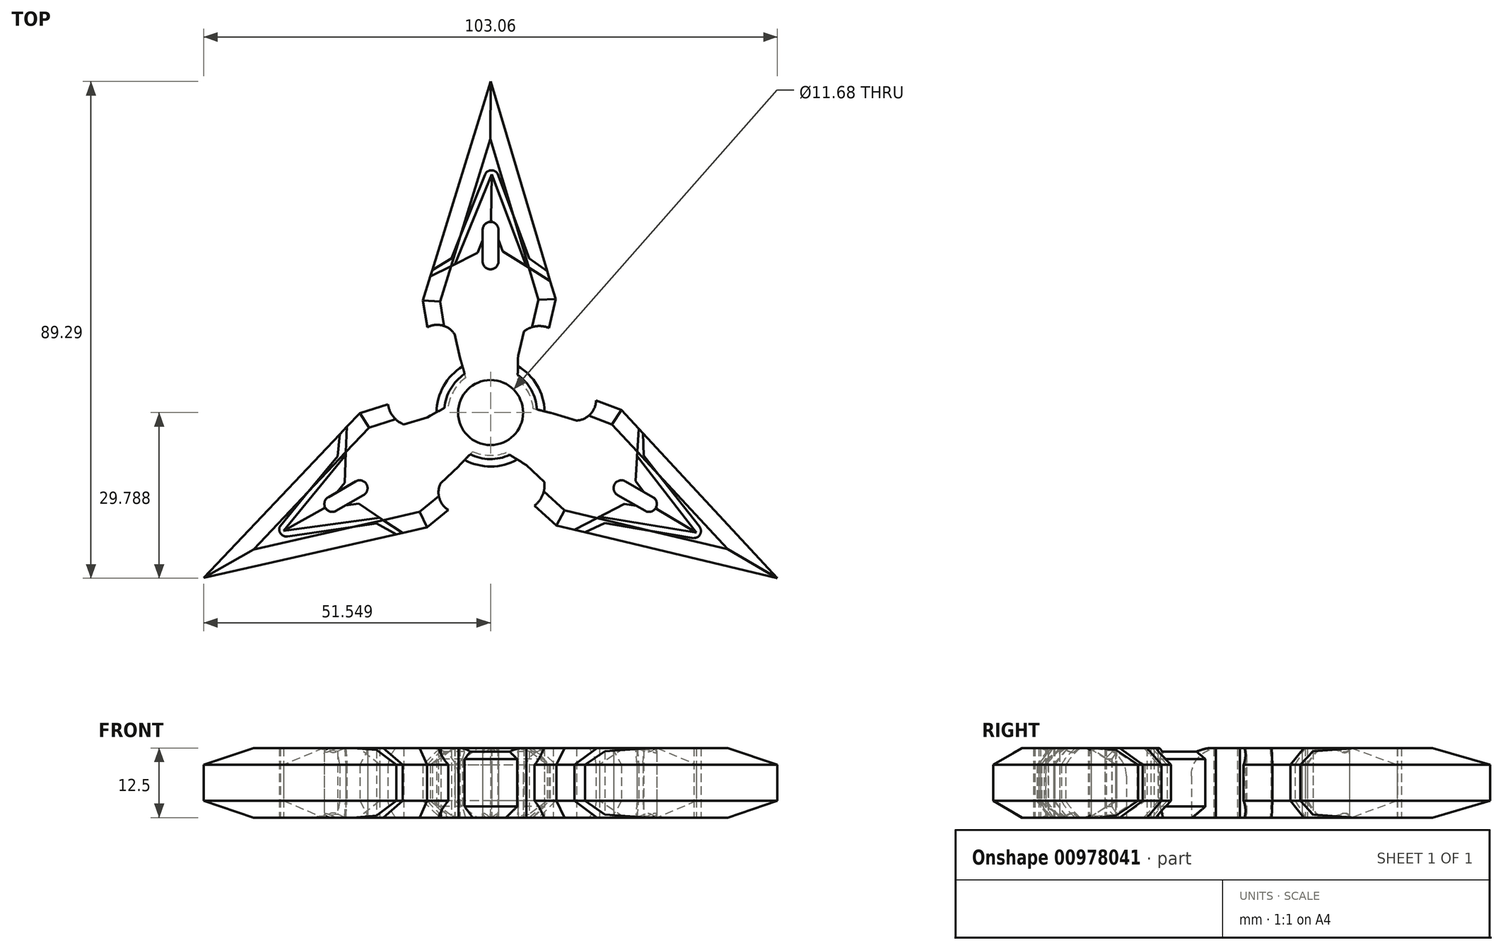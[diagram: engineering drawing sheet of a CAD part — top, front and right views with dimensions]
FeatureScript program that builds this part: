
annotation { "Feature Type Name" : "Feature", "Feature Type Description" : "" }
export const myFeature = defineFeature(function(context is Context, id is Id, definition is map)
    precondition{}
    {
        {
            var Q0;
            Q0=qCreatedBy(makeId("Top.planeOp"),FACE);
            var sketch = newSketch(context, id + "F0", { "sketchPlane" : qUnion([Q0])});
            skLineSegment(sketch, "E0", {"start": v(-184.92, 71.1) * mm, "end": v(-185.7, 75.95) * mm});
            skLineSegment(sketch, "E1", {"start": v(-185.7, 75.95) * mm, "end": v(-173.5, 115.3) * mm});
            skLineSegment(sketch, "E2", {"start": v(-173.5, 115.3) * mm, "end": v(-161.88, 76.16) * mm});
            skLineSegment(sketch, "E3", {"start": v(-161.88, 76.16) * mm, "end": v(-163.03, 71) * mm});
            skLineSegment(sketch, "E4", {"start": v(-167.58, 70.37) * mm, "end": v(-168.6, 66.06) * mm});
            skArc(sketch, "E5", {"start": v(-180.03, 69.88) * mm, "mid": v(-182.23, 71.45) * mm, "end": v(-184.92, 71.1) * mm});
            skArc(sketch, "E6", {"start": v(-163.03, 71) * mm, "mid": v(-165.39, 71.3) * mm, "end": v(-167.58, 70.37) * mm});
            skLineSegment(sketch, "E7", {"start": v(-180.03, 69.88) * mm, "end": v(-179.04, 65.65) * mm});
            skLineSegment(sketch, "E8.left", {"start": v(-172.13, 82.95) * mm, "end": v(-172.13, 88.64) * mm});
            skLineSegment(sketch, "E8.right", {"start": v(-174.97, 82.95) * mm, "end": v(-174.97, 88.64) * mm});
            skPoint(sketch, "E8.middle", {"position": v(-173.55, 85.8) * mm});
            skArc(sketch, "E9", {"start": v(-172.13, 88.64) * mm, "mid": v(-173.55, 90.06) * mm, "end": v(-174.97, 88.64) * mm});
            skArc(sketch, "E10", {"start": v(-174.97, 82.95) * mm, "mid": v(-173.55, 81.53) * mm, "end": v(-172.13, 82.95) * mm});
            skLineSegment(sketch, "E11", {"start": v(-184.36, 80.28) * mm, "end": v(-179.97, 82.46) * mm});
            skLineSegment(sketch, "E12", {"start": v(-179.97, 82.46) * mm, "end": v(-173.35, 98.59) * mm});
            skLineSegment(sketch, "E13", {"start": v(-173.35, 98.59) * mm, "end": v(-167.13, 82.12) * mm});
            skLineSegment(sketch, "E14", {"start": v(-167.13, 82.12) * mm, "end": v(-162.84, 79.4) * mm});
            skLineSegment(sketch, "E15", {"start": v(-162.84, 79.4) * mm, "end": v(-163.38, 81.23) * mm});
            skLineSegment(sketch, "E16", {"start": v(-163.38, 81.23) * mm, "end": v(-166.6, 83.5) * mm});
            skLineSegment(sketch, "E17", {"start": v(-166.6, 83.5) * mm, "end": v(-172.28, 98.69) * mm});
            skLineSegment(sketch, "E18", {"start": v(-184.02, 81.38) * mm, "end": v(-180.6, 83.48) * mm});
            skLineSegment(sketch, "E19", {"start": v(-180.6, 83.48) * mm, "end": v(-174.57, 98.54) * mm});
            skArc(sketch, "E20", {"start": v(-172.28, 98.69) * mm, "mid": v(-173.47, 99.33) * mm, "end": v(-174.57, 98.54) * mm});
            skArc(sketch, "E21", {"start": v(-178.6, 64.07) * mm, "mid": v(-181.98, 60.57) * mm, "end": v(-183.24, 55.86) * mm});
            skPoint(sketch, "E21.centerSnap0", {"position": v(-173.55, 81.53) * mm});
            skLineSegment(sketch, "E22.1.0", {"start": v(-184.94, 35.18) * mm, "end": v(-225.1, 26.07) * mm});
            skPoint(sketch, "E22.1.1", {"position": v(-195.84, 42.92) * mm});
            skPoint(sketch, "E22.1.3", {"position": v(-199.54, 40.78) * mm});
            skLineSegment(sketch, "E22.1.4", {"start": v(-201.02, 47.96) * mm, "end": v(-211.34, 35.44) * mm});
            skLineSegment(sketch, "E22.1.5", {"start": v(-225.1, 26.07) * mm, "end": v(-197.03, 55.71) * mm});
            skLineSegment(sketch, "E22.1.6", {"start": v(-194.02, 35.84) * mm, "end": v(-210.06, 33.53) * mm});
            skLineSegment(sketch, "E22.1.7", {"start": v(-210.72, 34.56) * mm, "end": v(-199.56, 48.18) * mm});
            skLineSegment(sketch, "E22.1.8", {"start": v(-189.17, 53.67) * mm, "end": v(-184.92, 54.94) * mm});
            skLineSegment(sketch, "E22.1.9", {"start": v(-193.44, 36.9) * mm, "end": v(-210.72, 34.56) * mm});
            skLineSegment(sketch, "E22.1.10", {"start": v(-197.03, 55.71) * mm, "end": v(-191.99, 57.29) * mm});
            skArc(sketch, "E22.1.11", {"start": v(-182.52, 43.14) * mm, "mid": v(-182.77, 40.44) * mm, "end": v(-181.13, 38.28) * mm});
            skArc(sketch, "E22.1.12", {"start": v(-191.99, 57.29) * mm, "mid": v(-191.07, 55.1) * mm, "end": v(-189.17, 53.67) * mm});
            skLineSegment(sketch, "E22.1.13", {"start": v(-190.48, 33.92) * mm, "end": v(-194.02, 35.84) * mm});
            skLineSegment(sketch, "E22.1.14", {"start": v(-200.67, 51.87) * mm, "end": v(-201.02, 47.96) * mm});
            skLineSegment(sketch, "E22.1.15", {"start": v(-181.13, 38.28) * mm, "end": v(-184.94, 35.18) * mm});
            skLineSegment(sketch, "E22.1.16", {"start": v(-189.36, 34.18) * mm, "end": v(-193.44, 36.9) * mm});
            skLineSegment(sketch, "E22.1.17", {"start": v(-182.52, 43.14) * mm, "end": v(-179.34, 46.1) * mm});
            skArc(sketch, "E22.1.18", {"start": v(-211.34, 35.44) * mm, "mid": v(-211.3, 34.09) * mm, "end": v(-210.06, 33.53) * mm});
            skLineSegment(sketch, "E22.1.19", {"start": v(-199.56, 48.18) * mm, "end": v(-199.36, 53.26) * mm});
            skLineSegment(sketch, "E22.1.20", {"start": v(-199.36, 53.26) * mm, "end": v(-200.67, 51.87) * mm});
            skLineSegment(sketch, "E22.1.21", {"start": v(-197.79, 43.44) * mm, "end": v(-202.71, 40.6) * mm});
            skArc(sketch, "E22.1.22", {"start": v(-202.71, 40.6) * mm, "mid": v(-203.23, 38.65) * mm, "end": v(-201.29, 38.13) * mm});
            skLineSegment(sketch, "E22.1.23", {"start": v(-196.37, 40.98) * mm, "end": v(-201.29, 38.13) * mm});
            skArc(sketch, "E22.1.24", {"start": v(-196.37, 40.98) * mm, "mid": v(-195.84, 42.92) * mm, "end": v(-197.79, 43.44) * mm});
            skLineSegment(sketch, "E22.2.0", {"start": v(-150.01, 56.23) * mm, "end": v(-122.04, 26) * mm});
            skPoint(sketch, "E22.2.1", {"position": v(-151.26, 42.92) * mm});
            skPoint(sketch, "E22.2.3", {"position": v(-147.56, 40.78) * mm});
            skLineSegment(sketch, "E22.2.4", {"start": v(-153.04, 35.9) * mm, "end": v(-137.04, 33.24) * mm});
            skLineSegment(sketch, "E22.2.5", {"start": v(-122.04, 26) * mm, "end": v(-161.74, 35.5) * mm});
            skLineSegment(sketch, "E22.2.6", {"start": v(-146.04, 48.04) * mm, "end": v(-136.02, 35.3) * mm});
            skLineSegment(sketch, "E22.2.7", {"start": v(-136.58, 34.22) * mm, "end": v(-153.96, 37.06) * mm});
            skLineSegment(sketch, "E22.2.8", {"start": v(-163.9, 43.32) * mm, "end": v(-167.13, 46.37) * mm});
            skLineSegment(sketch, "E22.2.9", {"start": v(-147.24, 48.01) * mm, "end": v(-136.58, 34.22) * mm});
            skLineSegment(sketch, "E22.2.10", {"start": v(-161.74, 35.5) * mm, "end": v(-165.63, 39.07) * mm});
            skArc(sketch, "E22.2.11", {"start": v(-158.11, 54.35) * mm, "mid": v(-155.65, 55.48) * mm, "end": v(-154.6, 57.98) * mm});
            skArc(sketch, "E22.2.12", {"start": v(-165.63, 39.07) * mm, "mid": v(-164.2, 40.96) * mm, "end": v(-163.9, 43.32) * mm});
            skLineSegment(sketch, "E22.2.13", {"start": v(-146.15, 52.06) * mm, "end": v(-146.04, 48.04) * mm});
            skLineSegment(sketch, "E22.2.14", {"start": v(-156.6, 34.26) * mm, "end": v(-153.04, 35.9) * mm});
            skLineSegment(sketch, "E22.2.15", {"start": v(-154.6, 57.98) * mm, "end": v(-150.01, 56.23) * mm});
            skLineSegment(sketch, "E22.2.16", {"start": v(-146.93, 52.9) * mm, "end": v(-147.24, 48.01) * mm});
            skLineSegment(sketch, "E22.2.17", {"start": v(-158.11, 54.35) * mm, "end": v(-162.27, 55.61) * mm});
            skArc(sketch, "E22.2.18", {"start": v(-137.04, 33.24) * mm, "mid": v(-135.88, 33.95) * mm, "end": v(-136.02, 35.3) * mm});
            skLineSegment(sketch, "E22.2.19", {"start": v(-153.96, 37.06) * mm, "end": v(-158.46, 34.7) * mm});
            skLineSegment(sketch, "E22.2.20", {"start": v(-158.46, 34.7) * mm, "end": v(-156.6, 34.26) * mm});
            skLineSegment(sketch, "E22.2.21", {"start": v(-150.74, 40.98) * mm, "end": v(-145.81, 38.13) * mm});
            skArc(sketch, "E22.2.22", {"start": v(-145.81, 38.13) * mm, "mid": v(-143.87, 38.65) * mm, "end": v(-144.4, 40.6) * mm});
            skLineSegment(sketch, "E22.2.23", {"start": v(-149.32, 43.44) * mm, "end": v(-144.4, 40.6) * mm});
            skArc(sketch, "E22.2.24", {"start": v(-149.32, 43.44) * mm, "mid": v(-151.26, 42.92) * mm, "end": v(-150.74, 40.98) * mm});
            skLineSegment(sketch, "E23", {"start": v(-184.92, 54.94) * mm, "end": v(-183.24, 55.86) * mm});
            skLineSegment(sketch, "E24", {"start": v(-179.34, 46.1) * mm, "end": v(-178.2, 47.28) * mm});
            skLineSegment(sketch, "E25.1.0", {"start": v(-167.13, 46.37) * mm, "end": v(-168.77, 47.36) * mm});
            skLineSegment(sketch, "E25.1.1", {"start": v(-162.27, 55.61) * mm, "end": v(-163.86, 56.01) * mm});
            skLineSegment(sketch, "E25.2.0", {"start": v(-168.6, 66.06) * mm, "end": v(-168.64, 64.15) * mm});
            skLineSegment(sketch, "E25.2.1", {"start": v(-179.04, 65.65) * mm, "end": v(-178.6, 64.07) * mm});
            skArc(sketch, "E26.trimOffspring", {"start": v(-178.2, 47.28) * mm, "mid": v(-173.47, 46.1) * mm, "end": v(-168.77, 47.36) * mm});
            skArc(sketch, "E27.trimOffspring", {"start": v(-163.86, 56.01) * mm, "mid": v(-165.2, 60.7) * mm, "end": v(-168.64, 64.15) * mm});
            skSolve(sketch);
        }
        {
            var Q0;
            {var subQ10=sQuery(id+"F0.wireOp",EDGE,"E0");Q0=makeQuery(id+"F0.imprint","IMPRINT",FACE,{"disambiguationData":[TD([[makeQuery(id+"F0.imprint","IMPRINT",EDGE,{"derivedFrom":subQ10}),-1.0]])]});}
            var Q1;
            {var subQ0=sQuery(id+"F0.wireOp",EDGE,"E16");Q1=makeQuery(id+"F0.imprint","IMPRINT",FACE,{"disambiguationData":[TD([[makeQuery(id+"F0.imprint","IMPRINT",EDGE,{"derivedFrom":subQ0}),-1.0]])]});}
            var Q2;
            Q2=makeQuery(id+"F0.imprint","IMPRINT",FACE,{"disambiguationData":[TD([[makeQuery(id+"F0.imprint","IMPRINT",EDGE,{"derivedFrom":sQuery(id+"F0.wireOp",EDGE,"E22.2.4")}),-1.0]])]});
            var Q3;
            Q3=makeQuery(id+"F0.imprint","IMPRINT",FACE,{"disambiguationData":[TD([[makeQuery(id+"F0.imprint","IMPRINT",EDGE,{"derivedFrom":sQuery(id+"F0.wireOp",EDGE,"E22.1.4")}),-1.0]])]});
            extrude(context, id + "F1", {"entities" : qUnion([Q0, Q1, Q2, Q3]), "depth" : 12.5 * mm, "offsetDistance" : 25 * mm});
        }
        {
            var Q0;
            {var subQ0=sQuery(id+"F0.wireOp",EDGE,"E22.1.0");Q0=makeQuery(id+"F1.opExtrude","CAP_EDGE",EDGE,{"disambiguationData":[OSD([subQ0]),TDD([makeQuery(id+"F0.imprint","IMPRINT",EDGE,{"disambiguationData":[TD([[makeQuery(id+"F0.imprint","INTERSECT",VERTEX,{"derivedFrom":[subQ0,sQuery(id+"F0.wireOp",EDGE,"E22.1.13")]}),-1.0]])],"derivedFrom":subQ0})])],"isStart":false});}
            var Q1;
            {var subQ0=sQuery(id+"F0.wireOp",EDGE,"E22.1.5");Q1=makeQuery(id+"F1.opExtrude","CAP_EDGE",EDGE,{"disambiguationData":[OSD([subQ0]),TDD([makeQuery(id+"F0.imprint","IMPRINT",EDGE,{"disambiguationData":[TD([[makeQuery(id+"F0.imprint","INTERSECT",VERTEX,{"derivedFrom":[sQuery(id+"F0.wireOp",EDGE,"E22.1.0"),subQ0]}),-1.0]])],"derivedFrom":subQ0})])],"isStart":false});}
            var Q2;
            {var subQ0=sQuery(id+"F0.wireOp",EDGE,"E22.2.5");Q2=makeQuery(id+"F1.opExtrude","CAP_EDGE",EDGE,{"disambiguationData":[OSD([subQ0]),TDD([makeQuery(id+"F0.imprint","IMPRINT",EDGE,{"disambiguationData":[TD([[makeQuery(id+"F0.imprint","INTERSECT",VERTEX,{"derivedFrom":[sQuery(id+"F0.wireOp",EDGE,"E22.2.0"),subQ0]}),-1.0]])],"derivedFrom":subQ0})])],"isStart":false});}
            var Q3;
            {var subQ0=sQuery(id+"F0.wireOp",EDGE,"E22.2.0");Q3=makeQuery(id+"F1.opExtrude","CAP_EDGE",EDGE,{"disambiguationData":[OSD([subQ0]),TDD([makeQuery(id+"F0.imprint","IMPRINT",EDGE,{"disambiguationData":[TD([[makeQuery(id+"F0.imprint","INTERSECT",VERTEX,{"derivedFrom":[subQ0,sQuery(id+"F0.wireOp",EDGE,"E22.2.13")]}),-1.0]])],"derivedFrom":subQ0})])],"isStart":false});}
            var Q4;
            {var subQ0=sQuery(id+"F0.wireOp",EDGE,"E1");Q4=makeQuery(id+"F1.opExtrude","CAP_EDGE",EDGE,{"disambiguationData":[OSD([subQ0]),TDD([makeQuery(id+"F0.imprint","IMPRINT",EDGE,{"disambiguationData":[TD([[makeQuery(id+"F0.imprint","INTERSECT",VERTEX,{"derivedFrom":[subQ0,sQuery(id+"F0.wireOp",EDGE,"E18")]}),-1.0]])],"derivedFrom":subQ0})])],"isStart":false});}
            var Q5;
            {var subQ0=sQuery(id+"F0.wireOp",EDGE,"E2");Q5=makeQuery(id+"F1.opExtrude","CAP_EDGE",EDGE,{"disambiguationData":[OSD([subQ0]),TDD([makeQuery(id+"F0.imprint","IMPRINT",EDGE,{"disambiguationData":[TD([[makeQuery(id+"F0.imprint","INTERSECT",VERTEX,{"derivedFrom":[sQuery(id+"F0.wireOp",EDGE,"E1"),subQ0]}),-1.0]])],"derivedFrom":subQ0})])],"isStart":false});}
            var Q6;
            {var subQ0=sQuery(id+"F0.wireOp",EDGE,"E2");Q6=makeQuery(id+"F1.opExtrude","CAP_EDGE",EDGE,{"disambiguationData":[OSD([subQ0]),TDD([makeQuery(id+"F0.imprint","IMPRINT",EDGE,{"disambiguationData":[TD([[makeQuery(id+"F0.imprint","INTERSECT",VERTEX,{"derivedFrom":[sQuery(id+"F0.wireOp",EDGE,"E1"),subQ0]}),-1.0]])],"derivedFrom":subQ0})])],"isStart":true});}
            var Q7;
            {var subQ0=sQuery(id+"F0.wireOp",EDGE,"E1");Q7=makeQuery(id+"F1.opExtrude","CAP_EDGE",EDGE,{"disambiguationData":[OSD([subQ0]),TDD([makeQuery(id+"F0.imprint","IMPRINT",EDGE,{"disambiguationData":[TD([[makeQuery(id+"F0.imprint","INTERSECT",VERTEX,{"derivedFrom":[subQ0,sQuery(id+"F0.wireOp",EDGE,"E18")]}),-1.0]])],"derivedFrom":subQ0})])],"isStart":true});}
            var Q8;
            {var subQ0=sQuery(id+"F0.wireOp",EDGE,"E22.2.0");Q8=makeQuery(id+"F1.opExtrude","CAP_EDGE",EDGE,{"disambiguationData":[OSD([subQ0]),TDD([makeQuery(id+"F0.imprint","IMPRINT",EDGE,{"disambiguationData":[TD([[makeQuery(id+"F0.imprint","INTERSECT",VERTEX,{"derivedFrom":[subQ0,sQuery(id+"F0.wireOp",EDGE,"E22.2.13")]}),-1.0]])],"derivedFrom":subQ0})])],"isStart":true});}
            var Q9;
            {var subQ0=sQuery(id+"F0.wireOp",EDGE,"E22.2.5");Q9=makeQuery(id+"F1.opExtrude","CAP_EDGE",EDGE,{"disambiguationData":[OSD([subQ0]),TDD([makeQuery(id+"F0.imprint","IMPRINT",EDGE,{"disambiguationData":[TD([[makeQuery(id+"F0.imprint","INTERSECT",VERTEX,{"derivedFrom":[sQuery(id+"F0.wireOp",EDGE,"E22.2.0"),subQ0]}),-1.0]])],"derivedFrom":subQ0})])],"isStart":true});}
            var Q10;
            {var subQ0=sQuery(id+"F0.wireOp",EDGE,"E22.1.0");Q10=makeQuery(id+"F1.opExtrude","CAP_EDGE",EDGE,{"disambiguationData":[OSD([subQ0]),TDD([makeQuery(id+"F0.imprint","IMPRINT",EDGE,{"disambiguationData":[TD([[makeQuery(id+"F0.imprint","INTERSECT",VERTEX,{"derivedFrom":[subQ0,sQuery(id+"F0.wireOp",EDGE,"E22.1.13")]}),-1.0]])],"derivedFrom":subQ0})])],"isStart":true});}
            var Q11;
            {var subQ0=sQuery(id+"F0.wireOp",EDGE,"E22.1.5");Q11=makeQuery(id+"F1.opExtrude","CAP_EDGE",EDGE,{"disambiguationData":[OSD([subQ0]),TDD([makeQuery(id+"F0.imprint","IMPRINT",EDGE,{"disambiguationData":[TD([[makeQuery(id+"F0.imprint","INTERSECT",VERTEX,{"derivedFrom":[sQuery(id+"F0.wireOp",EDGE,"E22.1.0"),subQ0]}),-1.0]])],"derivedFrom":subQ0})])],"isStart":true});}
            var Q12;
            {var subQ0=sQuery(id+"F0.wireOp",EDGE,"E22.2.5");Q12=makeQuery(id+"F1.opExtrude","CAP_EDGE",EDGE,{"disambiguationData":[OSD([subQ0]),TDD([makeQuery(id+"F0.imprint","IMPRINT",EDGE,{"disambiguationData":[TD([[makeQuery(id+"F0.imprint","INTERSECT",VERTEX,{"derivedFrom":[subQ0,sQuery(id+"F0.wireOp",EDGE,"E22.2.19")]}),-1.0]])],"derivedFrom":subQ0})])],"isStart":false});}
            var Q13;
            Q13=makeQuery(id+"F1.opExtrude","CAP_EDGE",EDGE,{"disambiguationData":[OSD([sQuery(id+"F0.wireOp",EDGE,"E22.2.10")])],"isStart":false});
            var Q14;
            Q14=makeQuery(id+"F1.opExtrude","CAP_EDGE",EDGE,{"disambiguationData":[OSD([sQuery(id+"F0.wireOp",EDGE,"E22.2.15")])],"isStart":false});
            var Q15;
            {var subQ0=sQuery(id+"F0.wireOp",EDGE,"E22.2.0");Q15=makeQuery(id+"F1.opExtrude","CAP_EDGE",EDGE,{"disambiguationData":[OSD([subQ0]),TDD([makeQuery(id+"F0.imprint","IMPRINT",EDGE,{"disambiguationData":[TD([[makeQuery(id+"F0.imprint","INTERSECT",VERTEX,{"derivedFrom":[subQ0,sQuery(id+"F0.wireOp",EDGE,"E22.2.15")]}),-1.0]])],"derivedFrom":subQ0})])],"isStart":false});}
            var Q16;
            Q16=makeQuery(id+"F1.opExtrude","CAP_EDGE",EDGE,{"disambiguationData":[OSD([sQuery(id+"F0.wireOp",EDGE,"E22.2.7")])],"isStart":false});
            var Q17;
            Q17=makeQuery(id+"F1.opExtrude","CAP_EDGE",EDGE,{"disambiguationData":[OSD([sQuery(id+"F0.wireOp",EDGE,"E22.2.9")])],"isStart":false});
            var Q18;
            Q18=makeQuery(id+"F1.opExtrude","CAP_EDGE",EDGE,{"disambiguationData":[OSD([sQuery(id+"F0.wireOp",EDGE,"E22.1.9")])],"isStart":false});
            var Q19;
            Q19=makeQuery(id+"F1.opExtrude","CAP_EDGE",EDGE,{"disambiguationData":[OSD([sQuery(id+"F0.wireOp",EDGE,"E22.1.7")])],"isStart":false});
            var Q20;
            Q20=makeQuery(id+"F1.opExtrude","CAP_EDGE",EDGE,{"disambiguationData":[OSD([sQuery(id+"F0.wireOp",EDGE,"E13")])],"isStart":false});
            var Q21;
            Q21=makeQuery(id+"F1.opExtrude","CAP_EDGE",EDGE,{"disambiguationData":[OSD([sQuery(id+"F0.wireOp",EDGE,"E12")])],"isStart":false});
            var Q22;
            Q22=makeQuery(id+"F1.opExtrude","CAP_EDGE",EDGE,{"disambiguationData":[OSD([sQuery(id+"F0.wireOp",EDGE,"E3")])],"isStart":false});
            var Q23;
            {var subQ0=sQuery(id+"F0.wireOp",EDGE,"E2");Q23=makeQuery(id+"F1.opExtrude","CAP_EDGE",EDGE,{"disambiguationData":[OSD([subQ0]),TDD([makeQuery(id+"F0.imprint","IMPRINT",EDGE,{"disambiguationData":[TD([[makeQuery(id+"F0.imprint","INTERSECT",VERTEX,{"derivedFrom":[subQ0,sQuery(id+"F0.wireOp",EDGE,"E14")]}),-1.0]])],"derivedFrom":subQ0})])],"isStart":false});}
            var Q24;
            {var subQ0=sQuery(id+"F0.wireOp",EDGE,"E22.1.0");Q24=makeQuery(id+"F1.opExtrude","CAP_EDGE",EDGE,{"disambiguationData":[OSD([subQ0]),TDD([makeQuery(id+"F0.imprint","IMPRINT",EDGE,{"disambiguationData":[TD([[makeQuery(id+"F0.imprint","INTERSECT",VERTEX,{"derivedFrom":[subQ0,sQuery(id+"F0.wireOp",EDGE,"E22.1.15")]}),-1.0]])],"derivedFrom":subQ0})])],"isStart":false});}
            var Q25;
            Q25=makeQuery(id+"F1.opExtrude","CAP_EDGE",EDGE,{"disambiguationData":[OSD([sQuery(id+"F0.wireOp",EDGE,"E22.1.15")])],"isStart":false});
            var Q26;
            {var subQ0=sQuery(id+"F0.wireOp",EDGE,"E22.1.5");Q26=makeQuery(id+"F1.opExtrude","CAP_EDGE",EDGE,{"disambiguationData":[OSD([subQ0]),TDD([makeQuery(id+"F0.imprint","IMPRINT",EDGE,{"disambiguationData":[TD([[makeQuery(id+"F0.imprint","INTERSECT",VERTEX,{"derivedFrom":[subQ0,sQuery(id+"F0.wireOp",EDGE,"E22.1.19")]}),-1.0]])],"derivedFrom":subQ0})])],"isStart":false});}
            var Q27;
            Q27=makeQuery(id+"F1.opExtrude","CAP_EDGE",EDGE,{"disambiguationData":[OSD([sQuery(id+"F0.wireOp",EDGE,"E22.1.10")])],"isStart":false});
            var Q28;
            Q28=makeQuery(id+"F1.opExtrude","CAP_EDGE",EDGE,{"disambiguationData":[OSD([sQuery(id+"F0.wireOp",EDGE,"E0")])],"isStart":false});
            var Q29;
            {var subQ0=sQuery(id+"F0.wireOp",EDGE,"E1");Q29=makeQuery(id+"F1.opExtrude","CAP_EDGE",EDGE,{"disambiguationData":[OSD([subQ0]),TDD([makeQuery(id+"F0.imprint","IMPRINT",EDGE,{"disambiguationData":[TD([[makeQuery(id+"F0.imprint","INTERSECT",VERTEX,{"derivedFrom":[sQuery(id+"F0.wireOp",EDGE,"E0"),subQ0]}),-1.0]])],"derivedFrom":subQ0})])],"isStart":false});}
            var Q30;
            {var subQ0=sQuery(id+"F0.wireOp",EDGE,"E1");Q30=makeQuery(id+"F1.opExtrude","CAP_EDGE",EDGE,{"disambiguationData":[OSD([subQ0]),TDD([makeQuery(id+"F0.imprint","IMPRINT",EDGE,{"disambiguationData":[TD([[makeQuery(id+"F0.imprint","INTERSECT",VERTEX,{"derivedFrom":[sQuery(id+"F0.wireOp",EDGE,"E0"),subQ0]}),-1.0]])],"derivedFrom":subQ0})])],"isStart":true});}
            var Q31;
            Q31=makeQuery(id+"F1.opExtrude","CAP_EDGE",EDGE,{"disambiguationData":[OSD([sQuery(id+"F0.wireOp",EDGE,"E0")])],"isStart":true});
            var Q32;
            Q32=makeQuery(id+"F1.opExtrude","CAP_EDGE",EDGE,{"disambiguationData":[OSD([sQuery(id+"F0.wireOp",EDGE,"E3")])],"isStart":true});
            var Q33;
            {var subQ0=sQuery(id+"F0.wireOp",EDGE,"E2");Q33=makeQuery(id+"F1.opExtrude","CAP_EDGE",EDGE,{"disambiguationData":[OSD([subQ0]),TDD([makeQuery(id+"F0.imprint","IMPRINT",EDGE,{"disambiguationData":[TD([[makeQuery(id+"F0.imprint","INTERSECT",VERTEX,{"derivedFrom":[subQ0,sQuery(id+"F0.wireOp",EDGE,"E14")]}),-1.0]])],"derivedFrom":subQ0})])],"isStart":true});}
            var Q34;
            Q34=makeQuery(id+"F1.opExtrude","CAP_EDGE",EDGE,{"disambiguationData":[OSD([sQuery(id+"F0.wireOp",EDGE,"E22.2.15")])],"isStart":true});
            var Q35;
            {var subQ0=sQuery(id+"F0.wireOp",EDGE,"E22.2.0");Q35=makeQuery(id+"F1.opExtrude","CAP_EDGE",EDGE,{"disambiguationData":[OSD([subQ0]),TDD([makeQuery(id+"F0.imprint","IMPRINT",EDGE,{"disambiguationData":[TD([[makeQuery(id+"F0.imprint","INTERSECT",VERTEX,{"derivedFrom":[subQ0,sQuery(id+"F0.wireOp",EDGE,"E22.2.15")]}),-1.0]])],"derivedFrom":subQ0})])],"isStart":true});}
            var Q36;
            Q36=makeQuery(id+"F1.opExtrude","CAP_EDGE",EDGE,{"disambiguationData":[OSD([sQuery(id+"F0.wireOp",EDGE,"E22.2.10")])],"isStart":true});
            var Q37;
            {var subQ0=sQuery(id+"F0.wireOp",EDGE,"E22.2.5");Q37=makeQuery(id+"F1.opExtrude","CAP_EDGE",EDGE,{"disambiguationData":[OSD([subQ0]),TDD([makeQuery(id+"F0.imprint","IMPRINT",EDGE,{"disambiguationData":[TD([[makeQuery(id+"F0.imprint","INTERSECT",VERTEX,{"derivedFrom":[subQ0,sQuery(id+"F0.wireOp",EDGE,"E22.2.19")]}),-1.0]])],"derivedFrom":subQ0})])],"isStart":true});}
            var Q38;
            {var subQ0=sQuery(id+"F0.wireOp",EDGE,"E22.1.0");Q38=makeQuery(id+"F1.opExtrude","CAP_EDGE",EDGE,{"disambiguationData":[OSD([subQ0]),TDD([makeQuery(id+"F0.imprint","IMPRINT",EDGE,{"disambiguationData":[TD([[makeQuery(id+"F0.imprint","INTERSECT",VERTEX,{"derivedFrom":[subQ0,sQuery(id+"F0.wireOp",EDGE,"E22.1.15")]}),-1.0]])],"derivedFrom":subQ0})])],"isStart":true});}
            var Q39;
            Q39=makeQuery(id+"F1.opExtrude","CAP_EDGE",EDGE,{"disambiguationData":[OSD([sQuery(id+"F0.wireOp",EDGE,"E22.1.15")])],"isStart":true});
            var Q40;
            {var subQ0=sQuery(id+"F0.wireOp",EDGE,"E22.1.5");Q40=makeQuery(id+"F1.opExtrude","CAP_EDGE",EDGE,{"disambiguationData":[OSD([subQ0]),TDD([makeQuery(id+"F0.imprint","IMPRINT",EDGE,{"disambiguationData":[TD([[makeQuery(id+"F0.imprint","INTERSECT",VERTEX,{"derivedFrom":[subQ0,sQuery(id+"F0.wireOp",EDGE,"E22.1.19")]}),-1.0]])],"derivedFrom":subQ0})])],"isStart":true});}
            var Q41;
            Q41=makeQuery(id+"F1.opExtrude","CAP_EDGE",EDGE,{"disambiguationData":[OSD([sQuery(id+"F0.wireOp",EDGE,"E22.1.10")])],"isStart":true});
            var Q42;
            Q42=makeQuery(id+"F1.opExtrude","CAP_EDGE",EDGE,{"disambiguationData":[OSD([sQuery(id+"F0.wireOp",EDGE,"E22.1.7")])],"isStart":true});
            var Q43;
            Q43=makeQuery(id+"F1.opExtrude","CAP_EDGE",EDGE,{"disambiguationData":[OSD([sQuery(id+"F0.wireOp",EDGE,"E22.1.9")])],"isStart":true});
            var Q44;
            Q44=makeQuery(id+"F1.opExtrude","CAP_EDGE",EDGE,{"disambiguationData":[OSD([sQuery(id+"F0.wireOp",EDGE,"E22.2.9")])],"isStart":true});
            var Q45;
            Q45=makeQuery(id+"F1.opExtrude","CAP_EDGE",EDGE,{"disambiguationData":[OSD([sQuery(id+"F0.wireOp",EDGE,"E22.2.7")])],"isStart":true});
            var Q46;
            Q46=makeQuery(id+"F1.opExtrude","CAP_EDGE",EDGE,{"disambiguationData":[OSD([sQuery(id+"F0.wireOp",EDGE,"E13")])],"isStart":true});
            var Q47;
            Q47=makeQuery(id+"F1.opExtrude","CAP_EDGE",EDGE,{"disambiguationData":[OSD([sQuery(id+"F0.wireOp",EDGE,"E12")])],"isStart":true});
            chamfer(context, id + "F2", {"entities" : qUnion([Q0, Q1, Q2, Q3, Q4, Q5, Q6, Q7, Q8, Q9, Q10, Q11, Q12, Q13, Q14, Q15, Q16, Q17, Q18, Q19, Q20, Q21, Q22, Q23, Q24, Q25, Q26, Q27, Q28, Q29, Q30, Q31, Q32, Q33, Q34, Q35, Q36, Q37, Q38, Q39, Q40, Q41, Q42, Q43, Q44, Q45, Q46, Q47]), "width" : 3 * mm, "tangentPropagation" : true});
        }
        {
            var Q0;
            Q0=makeQuery(id+"F0.imprint","IMPRINT",FACE,{"disambiguationData":[TD([[makeQuery(id+"F0.imprint","IMPRINT",EDGE,{"derivedFrom":sQuery(id+"F0.wireOp",EDGE,"E22.2.21")}),1.0]])]});
            var Q1;
            Q1=makeQuery(id+"F0.imprint","IMPRINT",FACE,{"disambiguationData":[TD([[makeQuery(id+"F0.imprint","IMPRINT",EDGE,{"derivedFrom":sQuery(id+"F0.wireOp",EDGE,"E8.left")}),1.0]])]});
            var Q2;
            Q2=makeQuery(id+"F0.imprint","IMPRINT",FACE,{"disambiguationData":[TD([[makeQuery(id+"F0.imprint","IMPRINT",EDGE,{"derivedFrom":sQuery(id+"F0.wireOp",EDGE,"E22.1.21")}),1.0]])]});
            extrude(context, id + "F3", {"entities" : qUnion([Q0, Q1, Q2]), "depth" : 12.5 * mm, "offsetDistance" : 25 * mm});
        }
        {
            var Q0;
            Q0=makeQuery(id+"F0.imprint","IMPRINT",FACE,{"disambiguationData":[TD([[makeQuery(id+"F0.imprint","IMPRINT",EDGE,{"derivedFrom":sQuery(id+"F0.wireOp",EDGE,"E22.2.4")}),1.0]])]});
            var Q1;
            {var subQ4=sQuery(id+"F0.wireOp",EDGE,"E11");Q1=makeQuery(id+"F0.imprint","IMPRINT",FACE,{"disambiguationData":[TD([[makeQuery(id+"F0.imprint","IMPRINT",EDGE,{"derivedFrom":subQ4}),1.0]])]});}
            var Q2;
            Q2=makeQuery(id+"F0.imprint","IMPRINT",FACE,{"disambiguationData":[TD([[makeQuery(id+"F0.imprint","IMPRINT",EDGE,{"derivedFrom":sQuery(id+"F0.wireOp",EDGE,"E22.1.4")}),1.0]])]});
            extrude(context, id + "F4", {"entities" : qUnion([Q0, Q1, Q2]), "depth" : 12.5 * mm, "offsetDistance" : 25 * mm});
        }
        {
            var Q0;
            Q0=makeQuery(id+"F4.opExtrude","CAP_EDGE",EDGE,{"disambiguationData":[OSD([sQuery(id+"F0.wireOp",EDGE,"E2")])],"isStart":false});
            var Q1;
            Q1=makeQuery(id+"F4.opExtrude","CAP_EDGE",EDGE,{"disambiguationData":[OSD([sQuery(id+"F0.wireOp",EDGE,"E2")])],"isStart":true});
            var Q2;
            Q2=makeQuery(id+"F4.opExtrude","CAP_EDGE",EDGE,{"disambiguationData":[OSD([sQuery(id+"F0.wireOp",EDGE,"E1")])],"isStart":false});
            var Q3;
            Q3=makeQuery(id+"F4.opExtrude","CAP_EDGE",EDGE,{"disambiguationData":[OSD([sQuery(id+"F0.wireOp",EDGE,"E1")])],"isStart":true});
            var Q4;
            Q4=makeQuery(id+"F4.opExtrude","CAP_EDGE",EDGE,{"disambiguationData":[OSD([sQuery(id+"F0.wireOp",EDGE,"E22.1.5")])],"isStart":false});
            var Q5;
            Q5=makeQuery(id+"F4.opExtrude","CAP_EDGE",EDGE,{"disambiguationData":[OSD([sQuery(id+"F0.wireOp",EDGE,"E22.1.5")])],"isStart":true});
            var Q6;
            Q6=makeQuery(id+"F4.opExtrude","CAP_EDGE",EDGE,{"disambiguationData":[OSD([sQuery(id+"F0.wireOp",EDGE,"E22.1.0")])],"isStart":false});
            var Q7;
            Q7=makeQuery(id+"F4.opExtrude","CAP_EDGE",EDGE,{"disambiguationData":[OSD([sQuery(id+"F0.wireOp",EDGE,"E22.1.0")])],"isStart":true});
            var Q8;
            Q8=makeQuery(id+"F4.opExtrude","CAP_EDGE",EDGE,{"disambiguationData":[OSD([sQuery(id+"F0.wireOp",EDGE,"E22.2.0")])],"isStart":true});
            var Q9;
            Q9=makeQuery(id+"F4.opExtrude","CAP_EDGE",EDGE,{"disambiguationData":[OSD([sQuery(id+"F0.wireOp",EDGE,"E22.2.0")])],"isStart":false});
            var Q10;
            Q10=makeQuery(id+"F4.opExtrude","CAP_EDGE",EDGE,{"disambiguationData":[OSD([sQuery(id+"F0.wireOp",EDGE,"E22.2.5")])],"isStart":true});
            var Q11;
            Q11=makeQuery(id+"F4.opExtrude","CAP_EDGE",EDGE,{"disambiguationData":[OSD([sQuery(id+"F0.wireOp",EDGE,"E22.2.5")])],"isStart":false});
            chamfer(context, id + "F5", {"entities" : qUnion([Q0, Q1, Q2, Q3, Q4, Q5, Q6, Q7, Q8, Q9, Q10, Q11]), "width" : 3 * mm, "tangentPropagation" : true});
        }
        {
            var Q0;
            Q0=makeQuery(id+"F2.opChamfer","SPLIT",FACE,{"disambiguationData":[OD(3.0)],"derivedFrom":makeQuery(id+"F1.opExtrude","CAP_FACE",FACE,{"disambiguationData":[OSD([sQuery(id+"F0.wireOp",EDGE,"E0"),sQuery(id+"F0.wireOp",EDGE,"E1"),sQuery(id+"F0.wireOp",EDGE,"E2"),sQuery(id+"F0.wireOp",EDGE,"E3"),sQuery(id+"F0.wireOp",EDGE,"E4"),sQuery(id+"F0.wireOp",EDGE,"E5"),sQuery(id+"F0.wireOp",EDGE,"E6"),sQuery(id+"F0.wireOp",EDGE,"E7"),sQuery(id+"F0.wireOp",EDGE,"E8.left"),sQuery(id+"F0.wireOp",EDGE,"E8.right"),sQuery(id+"F0.wireOp",EDGE,"E9"),sQuery(id+"F0.wireOp",EDGE,"E10"),sQuery(id+"F0.wireOp",EDGE,"E11"),sQuery(id+"F0.wireOp",EDGE,"E12"),sQuery(id+"F0.wireOp",EDGE,"E13"),sQuery(id+"F0.wireOp",EDGE,"E14"),sQuery(id+"F0.wireOp",EDGE,"E21"),sQuery(id+"F0.wireOp",EDGE,"E22.1.0"),sQuery(id+"F0.wireOp",EDGE,"E22.1.5"),sQuery(id+"F0.wireOp",EDGE,"E22.1.7"),sQuery(id+"F0.wireOp",EDGE,"E22.1.8"),sQuery(id+"F0.wireOp",EDGE,"E22.1.9"),sQuery(id+"F0.wireOp",EDGE,"E22.1.10"),sQuery(id+"F0.wireOp",EDGE,"E22.1.11"),sQuery(id+"F0.wireOp",EDGE,"E22.1.12"),sQuery(id+"F0.wireOp",EDGE,"E22.1.15"),sQuery(id+"F0.wireOp",EDGE,"E22.1.16"),sQuery(id+"F0.wireOp",EDGE,"E22.1.17"),sQuery(id+"F0.wireOp",EDGE,"E22.1.19"),sQuery(id+"F0.wireOp",EDGE,"E22.1.21"),sQuery(id+"F0.wireOp",EDGE,"E22.1.22"),sQuery(id+"F0.wireOp",EDGE,"E22.1.23"),sQuery(id+"F0.wireOp",EDGE,"E22.1.24"),sQuery(id+"F0.wireOp",EDGE,"E22.2.0"),sQuery(id+"F0.wireOp",EDGE,"E22.2.5"),sQuery(id+"F0.wireOp",EDGE,"E22.2.7"),sQuery(id+"F0.wireOp",EDGE,"E22.2.8"),sQuery(id+"F0.wireOp",EDGE,"E22.2.9"),sQuery(id+"F0.wireOp",EDGE,"E22.2.10"),sQuery(id+"F0.wireOp",EDGE,"E22.2.11"),sQuery(id+"F0.wireOp",EDGE,"E22.2.12"),sQuery(id+"F0.wireOp",EDGE,"E22.2.15"),sQuery(id+"F0.wireOp",EDGE,"E22.2.16"),sQuery(id+"F0.wireOp",EDGE,"E22.2.17"),sQuery(id+"F0.wireOp",EDGE,"E22.2.19"),sQuery(id+"F0.wireOp",EDGE,"E22.2.21"),sQuery(id+"F0.wireOp",EDGE,"E22.2.22"),sQuery(id+"F0.wireOp",EDGE,"E22.2.23"),sQuery(id+"F0.wireOp",EDGE,"E22.2.24"),sQuery(id+"F0.wireOp",EDGE,"E23"),sQuery(id+"F0.wireOp",EDGE,"E24"),sQuery(id+"F0.wireOp",EDGE,"E25.1.0"),sQuery(id+"F0.wireOp",EDGE,"E25.1.1"),sQuery(id+"F0.wireOp",EDGE,"E25.2.0"),sQuery(id+"F0.wireOp",EDGE,"E25.2.1"),sQuery(id+"F0.wireOp",EDGE,"E26.trimOffspring"),sQuery(id+"F0.wireOp",EDGE,"E27.trimOffspring")])],"isStart":true})});
            var sketch = newSketch(context, id + "F6", { "sketchPlane" : qUnion([Q0])});
            skCircle(sketch, "E28", {"center": v(-173.55, -55.79) * mm, "radius": 5.84 * mm});
            skSolve(sketch);
        }
        {
            var Q0;
            Q0 = qSketchRegion(id + "F6", true);
            extrude(context, id + "F7", {"entities" : qUnion([Q0]), "operationType" : NewBodyOperationType.REMOVE, "oppositeDirection" : true, "depth" : 25 * mm, "offsetDistance" : 25 * mm});
        }
        {
            var Q0;
            Q0=makeQuery(id+"F1.opExtrude","CAP_EDGE",EDGE,{"disambiguationData":[OSD([sQuery(id+"F0.wireOp",EDGE,"E26.trimOffspring")])],"isStart":true});
            var Q1;
            Q1=makeQuery(id+"F1.opExtrude","CAP_EDGE",EDGE,{"disambiguationData":[OSD([sQuery(id+"F0.wireOp",EDGE,"E21")])],"isStart":true});
            var Q2;
            Q2=makeQuery(id+"F1.opExtrude","CAP_EDGE",EDGE,{"disambiguationData":[OSD([sQuery(id+"F0.wireOp",EDGE,"E27.trimOffspring")])],"isStart":true});
            var Q3;
            Q3=makeQuery(id+"F1.opExtrude","CAP_EDGE",EDGE,{"disambiguationData":[OSD([sQuery(id+"F0.wireOp",EDGE,"E27.trimOffspring")])],"isStart":false});
            var Q4;
            Q4=makeQuery(id+"F1.opExtrude","CAP_EDGE",EDGE,{"disambiguationData":[OSD([sQuery(id+"F0.wireOp",EDGE,"E26.trimOffspring")])],"isStart":false});
            var Q5;
            Q5=makeQuery(id+"F1.opExtrude","CAP_EDGE",EDGE,{"disambiguationData":[OSD([sQuery(id+"F0.wireOp",EDGE,"E21")])],"isStart":false});
            chamfer(context, id + "F8", {"entities" : qUnion([Q0, Q1, Q2, Q3, Q4, Q5]), "width" : 2 * mm, "tangentPropagation" : true});
        }
        {
            var Q0;
            Q0=makeQuery(id+"F7.boolean.opBoolean","COPY",EDGE,{"derivedFrom":makeQuery(id+"F7.opExtrude","CAP_EDGE",EDGE,{"disambiguationData":[OSD([sQuery(id+"F6.wireOp",EDGE,"E28")])],"isStart":true})});
            var Q1;
            Q1=makeQuery(id+"F7.boolean.opBoolean","INTERSECT",EDGE,{"derivedFrom":[makeQuery(id+"F2.opChamfer","SPLIT",FACE,{"disambiguationData":[OD(3.0)],"derivedFrom":makeQuery(id+"F1.opExtrude","CAP_FACE",FACE,{"disambiguationData":[OSD([sQuery(id+"F0.wireOp",EDGE,"E0"),sQuery(id+"F0.wireOp",EDGE,"E1"),sQuery(id+"F0.wireOp",EDGE,"E2"),sQuery(id+"F0.wireOp",EDGE,"E3"),sQuery(id+"F0.wireOp",EDGE,"E4"),sQuery(id+"F0.wireOp",EDGE,"E5"),sQuery(id+"F0.wireOp",EDGE,"E6"),sQuery(id+"F0.wireOp",EDGE,"E7"),sQuery(id+"F0.wireOp",EDGE,"E8.left"),sQuery(id+"F0.wireOp",EDGE,"E8.right"),sQuery(id+"F0.wireOp",EDGE,"E9"),sQuery(id+"F0.wireOp",EDGE,"E10"),sQuery(id+"F0.wireOp",EDGE,"E11"),sQuery(id+"F0.wireOp",EDGE,"E12"),sQuery(id+"F0.wireOp",EDGE,"E13"),sQuery(id+"F0.wireOp",EDGE,"E14"),sQuery(id+"F0.wireOp",EDGE,"E21"),sQuery(id+"F0.wireOp",EDGE,"E22.1.0"),sQuery(id+"F0.wireOp",EDGE,"E22.1.5"),sQuery(id+"F0.wireOp",EDGE,"E22.1.7"),sQuery(id+"F0.wireOp",EDGE,"E22.1.8"),sQuery(id+"F0.wireOp",EDGE,"E22.1.9"),sQuery(id+"F0.wireOp",EDGE,"E22.1.10"),sQuery(id+"F0.wireOp",EDGE,"E22.1.11"),sQuery(id+"F0.wireOp",EDGE,"E22.1.12"),sQuery(id+"F0.wireOp",EDGE,"E22.1.15"),sQuery(id+"F0.wireOp",EDGE,"E22.1.16"),sQuery(id+"F0.wireOp",EDGE,"E22.1.17"),sQuery(id+"F0.wireOp",EDGE,"E22.1.19"),sQuery(id+"F0.wireOp",EDGE,"E22.1.21"),sQuery(id+"F0.wireOp",EDGE,"E22.1.22"),sQuery(id+"F0.wireOp",EDGE,"E22.1.23"),sQuery(id+"F0.wireOp",EDGE,"E22.1.24"),sQuery(id+"F0.wireOp",EDGE,"E22.2.0"),sQuery(id+"F0.wireOp",EDGE,"E22.2.5"),sQuery(id+"F0.wireOp",EDGE,"E22.2.7"),sQuery(id+"F0.wireOp",EDGE,"E22.2.8"),sQuery(id+"F0.wireOp",EDGE,"E22.2.9"),sQuery(id+"F0.wireOp",EDGE,"E22.2.10"),sQuery(id+"F0.wireOp",EDGE,"E22.2.11"),sQuery(id+"F0.wireOp",EDGE,"E22.2.12"),sQuery(id+"F0.wireOp",EDGE,"E22.2.15"),sQuery(id+"F0.wireOp",EDGE,"E22.2.16"),sQuery(id+"F0.wireOp",EDGE,"E22.2.17"),sQuery(id+"F0.wireOp",EDGE,"E22.2.19"),sQuery(id+"F0.wireOp",EDGE,"E22.2.21"),sQuery(id+"F0.wireOp",EDGE,"E22.2.22"),sQuery(id+"F0.wireOp",EDGE,"E22.2.23"),sQuery(id+"F0.wireOp",EDGE,"E22.2.24"),sQuery(id+"F0.wireOp",EDGE,"E23"),sQuery(id+"F0.wireOp",EDGE,"E24"),sQuery(id+"F0.wireOp",EDGE,"E25.1.0"),sQuery(id+"F0.wireOp",EDGE,"E25.1.1"),sQuery(id+"F0.wireOp",EDGE,"E25.2.0"),sQuery(id+"F0.wireOp",EDGE,"E25.2.1"),sQuery(id+"F0.wireOp",EDGE,"E26.trimOffspring"),sQuery(id+"F0.wireOp",EDGE,"E27.trimOffspring")])],"isStart":false})}),makeQuery(id+"F7.opExtrude","SWEPT_FACE",FACE,{"disambiguationData":[OSD([sQuery(id+"F6.wireOp",EDGE,"E28")])]})]});
            fillet(context, id + "F9", {"entities" : qUnion([Q0, Q1]), "radius" : 5 * mm, "tangentPropagation" : true, "allowEdgeOverflow" : false});
        }
        {
            var Q0;
            Q0=makeQuery(id+"F3.opExtrude","CAP_EDGE",EDGE,{"disambiguationData":[OSD([sQuery(id+"F0.wireOp",EDGE,"E22.1.22")])],"isStart":false});
            var Q1;
            Q1=makeQuery(id+"F3.opExtrude","CAP_EDGE",EDGE,{"disambiguationData":[OSD([sQuery(id+"F0.wireOp",EDGE,"E9")])],"isStart":false});
            var Q2;
            Q2=makeQuery(id+"F3.opExtrude","CAP_EDGE",EDGE,{"disambiguationData":[OSD([sQuery(id+"F0.wireOp",EDGE,"E22.2.22")])],"isStart":false});
            var Q3;
            Q3=makeQuery(id+"F3.opExtrude","CAP_EDGE",EDGE,{"disambiguationData":[OSD([sQuery(id+"F0.wireOp",EDGE,"E22.2.22")])],"isStart":true});
            var Q4;
            Q4=makeQuery(id+"F3.opExtrude","CAP_EDGE",EDGE,{"disambiguationData":[OSD([sQuery(id+"F0.wireOp",EDGE,"E9")])],"isStart":true});
            var Q5;
            Q5=makeQuery(id+"F3.opExtrude","CAP_EDGE",EDGE,{"disambiguationData":[OSD([sQuery(id+"F0.wireOp",EDGE,"E22.1.22")])],"isStart":true});
            fillet(context, id + "F10", {"entities" : qUnion([Q0, Q1, Q2, Q3, Q4, Q5]), "radius" : 1 * mm, "tangentPropagation" : true, "allowEdgeOverflow" : false});
        }
    });
